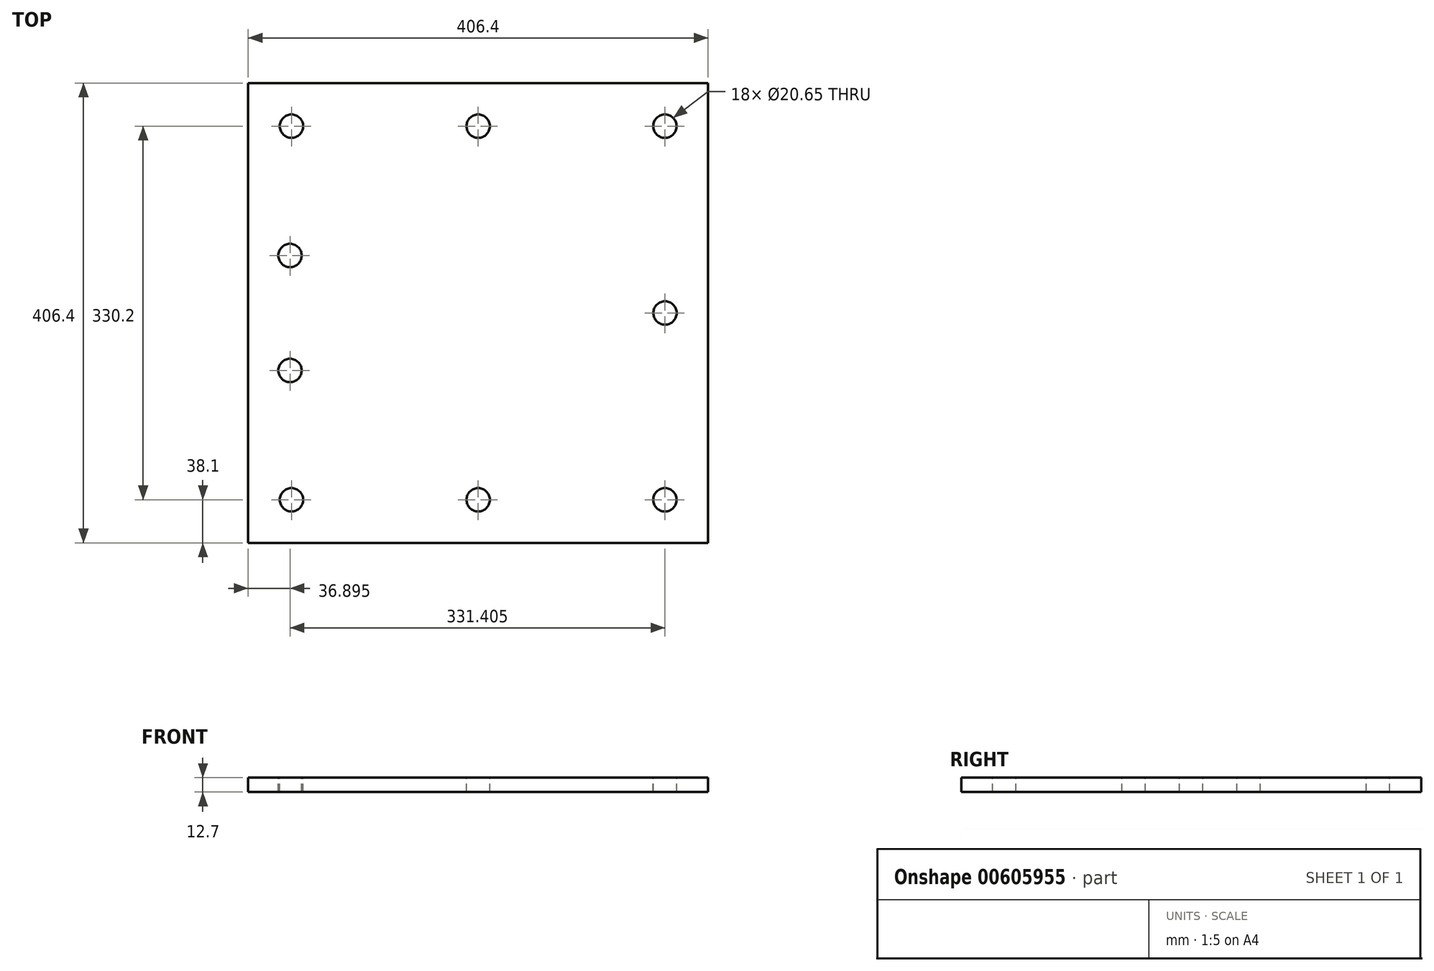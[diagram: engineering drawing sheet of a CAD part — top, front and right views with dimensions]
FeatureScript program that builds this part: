
annotation { "Feature Type Name" : "Feature", "Feature Type Description" : "" }
export const myFeature = defineFeature(function(context is Context, id is Id, definition is map)
    precondition{}
    {
        {
            var Q0;
            Q0=qCreatedBy(makeId("Top.planeOp"),FACE);
            var sketch = newSketch(context, id + "F0", { "sketchPlane" : qUnion([Q0])});
            skLineSegment(sketch, "E0.bottom", {"start": v(203.2, -203.2) * mm, "end": v(-203.2, -203.2) * mm});
            skLineSegment(sketch, "E0.top", {"start": v(203.2, 203.2) * mm, "end": v(-203.2, 203.2) * mm});
            skLineSegment(sketch, "E0.left", {"start": v(203.2, -203.2) * mm, "end": v(203.2, 203.2) * mm});
            skLineSegment(sketch, "E0.right", {"start": v(-203.2, -203.2) * mm, "end": v(-203.2, 203.2) * mm});
            skPoint(sketch, "E0.middle", {"position": v(0, 0) * mm});
            skSolve(sketch);
        }
        {
            var Q0;
            Q0 = qSketchRegion(id + "F0", true);
            extrude(context, id + "F1", {"entities" : qUnion([Q0]), "depth" : 12.7 * mm, "offsetDistance" : 25.4 * mm});
        }
        {
            var Q0;
            Q0=makeQuery(id+"F1.opExtrude","CAP_FACE",FACE,{"disambiguationData":[OSD([sQuery(id+"F0.wireOp",EDGE,"E0.bottom"),sQuery(id+"F0.wireOp",EDGE,"E0.top"),sQuery(id+"F0.wireOp",EDGE,"E0.left"),sQuery(id+"F0.wireOp",EDGE,"E0.right")])],"isStart":false});
            var sketch = newSketch(context, id + "F2", { "sketchPlane" : qUnion([Q0])});
            skCircle(sketch, "E1", {"center": v(-164.98, 165.1) * mm, "radius": 10.33 * mm});
            skCircle(sketch, "E2", {"center": v(-166.3, 50.8) * mm, "radius": 10.33 * mm});
            skCircle(sketch, "E3.MirrorC", {"center": v(-166.3, -50.8) * mm, "radius": 10.33 * mm});
            skCircle(sketch, "E4.MirrorC", {"center": v(-164.98, -165.1) * mm, "radius": 10.33 * mm});
            skCircle(sketch, "E5.MirrorC", {"center": v(164.98, 165.1) * mm, "radius": 10.33 * mm});
            skCircle(sketch, "E6.MirrorC", {"center": v(164.98, -165.1) * mm, "radius": 10.33 * mm});
            skCircle(sketch, "E7", {"center": v(165.1, 0) * mm, "radius": 10.33 * mm});
            skCircle(sketch, "E8", {"center": v(0, 165.1) * mm, "radius": 10.33 * mm});
            skCircle(sketch, "E9.MirrorC", {"center": v(0, -165.1) * mm, "radius": 10.33 * mm});
            skSolve(sketch);
        }
        {
            var Q0;
            Q0 = qSketchRegion(id + "F2", true);
            extrude(context, id + "F3", {"entities" : qUnion([Q0]), "operationType" : NewBodyOperationType.REMOVE, "oppositeDirection" : true, "depth" : 25.4 * mm, "offsetDistance" : 25.4 * mm});
        }
    });
